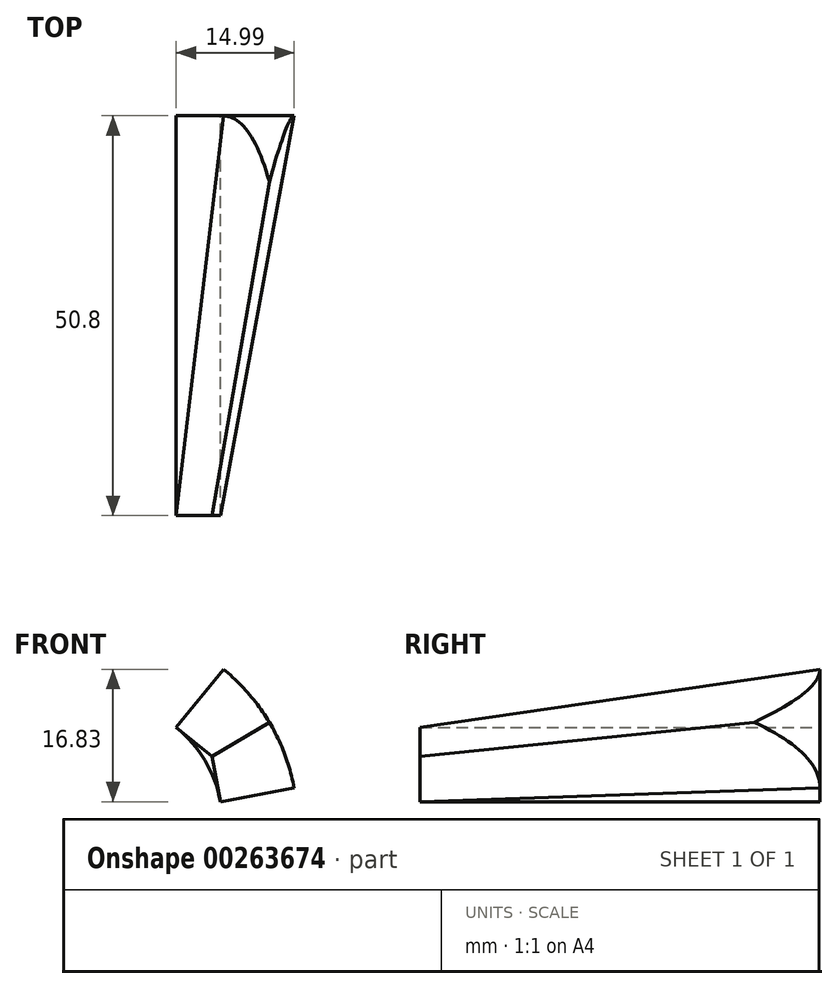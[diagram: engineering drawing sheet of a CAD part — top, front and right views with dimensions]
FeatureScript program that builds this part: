
annotation { "Feature Type Name" : "Feature", "Feature Type Description" : "" }
export const myFeature = defineFeature(function(context is Context, id is Id, definition is map)
    precondition{}
    {
        {
            var Q0;
            Q0=qCreatedBy(makeId("Front.planeOp"),FACE);
            var sketch = newSketch(context, id + "F0", { "sketchPlane" : qUnion([Q0])});
            skCircle(sketch, "E0", {"center": v(0, 0) * mm, "radius": 25.4 * mm});
            skCircle(sketch, "E1", {"center": v(0, 0) * mm, "radius": 15.88 * mm});
            skCircle(sketch, "E2", {"center": v(0, 0) * mm, "radius": 9.53 * mm});
            skLineSegment(sketch, "E3", {"start": v(15.97, 19.75) * mm, "end": v(-15.97, -19.75) * mm});
            skLineSegment(sketch, "E4", {"start": v(-15.93, 19.78) * mm, "end": v(16.53, -19.3) * mm});
            skLineSegment(sketch, "E5", {"start": v(0, 0) * mm, "end": v(-24.97, 4.67) * mm});
            skLineSegment(sketch, "E6", {"start": v(0, 0) * mm, "end": v(-22.89, -11.02) * mm});
            skLineSegment(sketch, "E7", {"start": v(0, 0) * mm, "end": v(24.97, 4.67) * mm});
            skLineSegment(sketch, "E8", {"start": v(0, 0) * mm, "end": v(23.96, -8.44) * mm});
            skSolve(sketch);
        }
        {
            var Q0;
            {var subQ0=sQuery(id+"F0.wireOp",EDGE,"E4");var subQ1=sQuery(id+"F0.wireOp",EDGE,"E0");var subQ2=makeQuery(id+"F0.imprint","INTERSECT",VERTEX,{"disambiguationData":[OD(0.0)],"derivedFrom":[subQ1,subQ0]});Q0=makeQuery(id+"F0.imprint","IMPRINT",FACE,{"disambiguationData":[TD([[makeQuery(id+"F0.imprint","IMPRINT",EDGE,{"disambiguationData":[TD([[subQ2,-1.0]])],"derivedFrom":subQ1}),1.0]])]});}
            var Q1;
            {var subQ0=sQuery(id+"F0.wireOp",EDGE,"E4");var subQ1=sQuery(id+"F0.wireOp",EDGE,"E1");var subQ2=makeQuery(id+"F0.imprint","INTERSECT",VERTEX,{"disambiguationData":[OD(0.0)],"derivedFrom":[subQ1,subQ0]});Q1=makeQuery(id+"F0.imprint","IMPRINT",FACE,{"disambiguationData":[TD([[makeQuery(id+"F0.imprint","IMPRINT",EDGE,{"disambiguationData":[TD([[subQ2,-1.0]])],"derivedFrom":subQ1}),1.0]])]});}
            var Q2;
            {var subQ0=sQuery(id+"F0.wireOp",EDGE,"E3");var subQ1=sQuery(id+"F0.wireOp",EDGE,"E1");var subQ2=makeQuery(id+"F0.imprint","INTERSECT",VERTEX,{"disambiguationData":[OD(0.0)],"derivedFrom":[subQ1,subQ0]});Q2=makeQuery(id+"F0.imprint","IMPRINT",FACE,{"disambiguationData":[TD([[makeQuery(id+"F0.imprint","IMPRINT",EDGE,{"disambiguationData":[TD([[subQ2,-1.0]])],"derivedFrom":subQ1}),1.0]])]});}
            var Q3;
            {var subQ0=sQuery(id+"F0.wireOp",EDGE,"E3");var subQ1=sQuery(id+"F0.wireOp",EDGE,"E1");var subQ2=makeQuery(id+"F0.imprint","INTERSECT",VERTEX,{"disambiguationData":[OD(0.0)],"derivedFrom":[subQ1,subQ0]});Q3=makeQuery(id+"F0.imprint","IMPRINT",FACE,{"disambiguationData":[TD([[makeQuery(id+"F0.imprint","IMPRINT",EDGE,{"disambiguationData":[TD([[subQ2,1.0]])],"derivedFrom":subQ1}),1.0]])]});}
            var Q4;
            {var subQ0=sQuery(id+"F0.wireOp",EDGE,"E7");var subQ1=sQuery(id+"F0.wireOp",EDGE,"E1");var subQ2=makeQuery(id+"F0.imprint","INTERSECT",VERTEX,{"derivedFrom":[subQ1,subQ0]});Q4=makeQuery(id+"F0.imprint","IMPRINT",FACE,{"disambiguationData":[TD([[makeQuery(id+"F0.imprint","IMPRINT",EDGE,{"disambiguationData":[TD([[subQ2,1.0]])],"derivedFrom":subQ1}),1.0]])]});}
            var Q5;
            {var subQ0=sQuery(id+"F0.wireOp",EDGE,"E4");var subQ1=sQuery(id+"F0.wireOp",EDGE,"E1");var subQ2=makeQuery(id+"F0.imprint","INTERSECT",VERTEX,{"disambiguationData":[OD(1.0)],"derivedFrom":[subQ1,subQ0]});Q5=makeQuery(id+"F0.imprint","IMPRINT",FACE,{"disambiguationData":[TD([[makeQuery(id+"F0.imprint","IMPRINT",EDGE,{"disambiguationData":[TD([[subQ2,-1.0]])],"derivedFrom":subQ1}),1.0]])]});}
            var Q6;
            {var subQ0=sQuery(id+"F0.wireOp",EDGE,"E3");var subQ1=sQuery(id+"F0.wireOp",EDGE,"E1");var subQ2=makeQuery(id+"F0.imprint","INTERSECT",VERTEX,{"disambiguationData":[OD(1.0)],"derivedFrom":[subQ1,subQ0]});Q6=makeQuery(id+"F0.imprint","IMPRINT",FACE,{"disambiguationData":[TD([[makeQuery(id+"F0.imprint","IMPRINT",EDGE,{"disambiguationData":[TD([[subQ2,-1.0]])],"derivedFrom":subQ1}),1.0]])]});}
            var Q7;
            {var subQ0=sQuery(id+"F0.wireOp",EDGE,"E6");var subQ1=sQuery(id+"F0.wireOp",EDGE,"E1");var subQ2=makeQuery(id+"F0.imprint","INTERSECT",VERTEX,{"derivedFrom":[subQ1,subQ0]});Q7=makeQuery(id+"F0.imprint","IMPRINT",FACE,{"disambiguationData":[TD([[makeQuery(id+"F0.imprint","IMPRINT",EDGE,{"disambiguationData":[TD([[subQ2,-1.0]])],"derivedFrom":subQ1}),1.0]])]});}
            var Q8;
            {var subQ0=sQuery(id+"F0.wireOp",EDGE,"E5");var subQ1=sQuery(id+"F0.wireOp",EDGE,"E1");var subQ2=makeQuery(id+"F0.imprint","INTERSECT",VERTEX,{"derivedFrom":[subQ1,subQ0]});Q8=makeQuery(id+"F0.imprint","IMPRINT",FACE,{"disambiguationData":[TD([[makeQuery(id+"F0.imprint","IMPRINT",EDGE,{"disambiguationData":[TD([[subQ2,-1.0]])],"derivedFrom":subQ1}),1.0]])]});}
            var Q9;
            {var subQ0=sQuery(id+"F0.wireOp",EDGE,"E3");var subQ1=sQuery(id+"F0.wireOp",EDGE,"E0");var subQ2=makeQuery(id+"F0.imprint","INTERSECT",VERTEX,{"disambiguationData":[OD(0.0)],"derivedFrom":[subQ1,subQ0]});Q9=makeQuery(id+"F0.imprint","IMPRINT",FACE,{"disambiguationData":[TD([[makeQuery(id+"F0.imprint","IMPRINT",EDGE,{"disambiguationData":[TD([[subQ2,1.0]])],"derivedFrom":subQ1}),1.0]])]});}
            var Q10;
            {var subQ0=sQuery(id+"F0.wireOp",EDGE,"E3");var subQ1=sQuery(id+"F0.wireOp",EDGE,"E0");var subQ2=makeQuery(id+"F0.imprint","INTERSECT",VERTEX,{"disambiguationData":[OD(1.0)],"derivedFrom":[subQ1,subQ0]});Q10=makeQuery(id+"F0.imprint","IMPRINT",FACE,{"disambiguationData":[TD([[makeQuery(id+"F0.imprint","IMPRINT",EDGE,{"disambiguationData":[TD([[subQ2,1.0]])],"derivedFrom":subQ1}),1.0]])]});}
            var Q11;
            {var subQ0=sQuery(id+"F0.wireOp",EDGE,"E8");var subQ1=sQuery(id+"F0.wireOp",EDGE,"E0");var subQ2=makeQuery(id+"F0.imprint","INTERSECT",VERTEX,{"derivedFrom":[subQ1,subQ0]});Q11=makeQuery(id+"F0.imprint","IMPRINT",FACE,{"disambiguationData":[TD([[makeQuery(id+"F0.imprint","IMPRINT",EDGE,{"disambiguationData":[TD([[subQ2,1.0]])],"derivedFrom":subQ1}),1.0]])]});}
            extrude(context, id + "F1", {"entities" : qUnion([Q0, Q1, Q2, Q3, Q4, Q5, Q6, Q7, Q8, Q9, Q10, Q11]), "depth" : 50.8 * mm});
        }
        {
            var Q0;
            Q0=makeQuery(id+"F1.opExtrude","CAP_FACE",FACE,{"disambiguationData":[OSD([sQuery(id+"F0.wireOp",EDGE,"E0"),sQuery(id+"F0.wireOp",EDGE,"E1"),sQuery(id+"F0.wireOp",EDGE,"E2"),sQuery(id+"F0.wireOp",EDGE,"E3"),sQuery(id+"F0.wireOp",EDGE,"E4"),sQuery(id+"F0.wireOp",EDGE,"E5"),sQuery(id+"F0.wireOp",EDGE,"E6"),sQuery(id+"F0.wireOp",EDGE,"E7"),sQuery(id+"F0.wireOp",EDGE,"E8")])],"isStart":false});
            var sketch = newSketch(context, id + "F2", { "sketchPlane" : qUnion([Q0])});
            skLineSegment(sketch, "E9", {"start": v(0, 0) * mm, "end": v(-9.53, 0) * mm});
            skLineSegment(sketch, "E10", {"start": v(0, 0) * mm, "end": v(9.53, 0) * mm});
            skLineSegment(sketch, "E11", {"start": v(0, 0) * mm, "end": v(0, 9.53) * mm});
            skLineSegment(sketch, "E12", {"start": v(0, 0) * mm, "end": v(0, -9.53) * mm});
            skLineSegment(sketch, "E13", {"start": v(0, 0) * mm, "end": v(6.74, 6.74) * mm});
            skLineSegment(sketch, "E14", {"start": v(0, 0) * mm, "end": v(-6.74, 6.74) * mm});
            skLineSegment(sketch, "E15", {"start": v(-6.74, 6.74) * mm, "end": v(-9.53, 9.52) * mm});
            skLineSegment(sketch, "E16", {"start": v(-9.53, 9.52) * mm, "end": v(-9.53, 0) * mm});
            skLineSegment(sketch, "E17", {"start": v(6.74, 6.74) * mm, "end": v(9.53, 9.52) * mm});
            skLineSegment(sketch, "E18", {"start": v(9.53, 9.52) * mm, "end": v(9.53, 0) * mm});
            skSolve(sketch);
        }
        {
            var Q0;
            {var subQ0=sQuery(id+"F2.wireOp",EDGE,"E15");Q0=makeQuery(id+"F2.imprint","IMPRINT",FACE,{"disambiguationData":[TD([[makeQuery(id+"F2.imprint","IMPRINT",EDGE,{"derivedFrom":subQ0}),1.0]])]});}
            var Q1;
            {var subQ0=sQuery(id+"F2.wireOp",EDGE,"E17");Q1=makeQuery(id+"F2.imprint","IMPRINT",FACE,{"disambiguationData":[TD([[makeQuery(id+"F2.imprint","IMPRINT",EDGE,{"derivedFrom":subQ0}),-1.0]])]});}
            extrude(context, id + "F3", {"entities" : qUnion([Q0, Q1]), "operationType" : NewBodyOperationType.REMOVE, "oppositeDirection" : true, "depth" : 50.8 * mm});
        }
        {
            var Q0;
            {var subQ0=sQuery(id+"F0.wireOp",EDGE,"E3");Q0=makeQuery(id+"F1.opExtrude","SWEPT_FACE",FACE,{"disambiguationData":[OSD([subQ0]),TDD([makeQuery(id+"F0.imprint","IMPRINT",EDGE,{"disambiguationData":[TD([[makeQuery(id+"F0.imprint","INTERSECT",VERTEX,{"disambiguationData":[OD(1.0)],"derivedFrom":[sQuery(id+"F0.wireOp",EDGE,"E0"),subQ0]}),1.0]])],"derivedFrom":subQ0})])]});}
            var sketch = newSketch(context, id + "F4", { "sketchPlane" : qUnion([Q0])});
            skLineSegment(sketch, "E19", {"start": v(-50.8, -15.88) * mm, "end": v(0, -25.4) * mm});
            skSolve(sketch);
        }
        {
            var Q0;
            Q0=makeQuery(id+"F4.imprint","IMPRINT",FACE,{"disambiguationData":[TD([[makeQuery(id+"F4.imprint","IMPRINT",EDGE,{"derivedFrom":sQuery(id+"F4.wireOp",EDGE,"E19")}),-1.0]])]});
            extrude(context, id + "F5", {"entities" : qUnion([Q0]), "operationType" : NewBodyOperationType.REMOVE, "endBound" : BoundingType.THROUGH_ALL, "oppositeDirection" : true, "depth" : 25.4 * mm});
        }
        {
            var Q0;
            Q0=makeQuery(id+"F1.opExtrude","SWEPT_FACE",FACE,{"disambiguationData":[OSD([sQuery(id+"F0.wireOp",EDGE,"E6")])]});
            var sketch = newSketch(context, id + "F6", { "sketchPlane" : qUnion([Q0])});
            skLineSegment(sketch, "E20", {"start": v(-15.87, -50.8) * mm, "end": v(-25.4, 0) * mm});
            skSolve(sketch);
        }
        {
            var Q0;
            Q0 = qSketchRegion(id + "F6", true);
            var Q1;
            Q1=makeQuery(id+"F6.imprint","IMPRINT",FACE,{"disambiguationData":[TD([[makeQuery(id+"F6.imprint","IMPRINT",EDGE,{"derivedFrom":sQuery(id+"F6.wireOp",EDGE,"E20")}),1.0]])]});
            extrude(context, id + "F7", {"entities" : qUnion([Q0, Q1]), "operationType" : NewBodyOperationType.REMOVE, "endBound" : BoundingType.THROUGH_ALL, "oppositeDirection" : true, "depth" : 25.4 * mm});
        }
        {
            var Q0;
            {var subQ0=sQuery(id+"F0.wireOp",EDGE,"E4");Q0=makeQuery(id+"F1.opExtrude","SWEPT_FACE",FACE,{"disambiguationData":[OSD([subQ0]),TDD([makeQuery(id+"F0.imprint","IMPRINT",EDGE,{"disambiguationData":[TD([[makeQuery(id+"F0.imprint","INTERSECT",VERTEX,{"disambiguationData":[OD(1.0)],"derivedFrom":[sQuery(id+"F0.wireOp",EDGE,"E0"),subQ0]}),1.0]])],"derivedFrom":subQ0})])]});}
            var sketch = newSketch(context, id + "F8", { "sketchPlane" : qUnion([Q0])});
            skLineSegment(sketch, "E21", {"start": v(50.8, -15.87) * mm, "end": v(0, -25.4) * mm});
            skSolve(sketch);
        }
        {
            var Q0;
            Q0 = qSketchRegion(id + "F8", true);
            var Q1;
            Q1=makeQuery(id+"F8.imprint","IMPRINT",FACE,{"disambiguationData":[TD([[makeQuery(id+"F8.imprint","IMPRINT",EDGE,{"derivedFrom":sQuery(id+"F8.wireOp",EDGE,"E21")}),1.0]])]});
            extrude(context, id + "F9", {"entities" : qUnion([Q0, Q1]), "operationType" : NewBodyOperationType.REMOVE, "endBound" : BoundingType.THROUGH_ALL, "oppositeDirection" : true, "depth" : 25.4 * mm});
        }
        {
            var Q0;
            Q0=makeQuery(id+"F1.opExtrude","SWEPT_FACE",FACE,{"disambiguationData":[OSD([sQuery(id+"F0.wireOp",EDGE,"E8")])]});
            var sketch = newSketch(context, id + "F10", { "sketchPlane" : qUnion([Q0])});
            skLineSegment(sketch, "E22", {"start": v(15.88, -50.8) * mm, "end": v(25.4, 0) * mm});
            skSolve(sketch);
        }
        {
            var Q0;
            Q0 = qSketchRegion(id + "F10", true);
            var Q1;
            Q1=makeQuery(id+"F10.imprint","IMPRINT",FACE,{"disambiguationData":[TD([[makeQuery(id+"F10.imprint","IMPRINT",EDGE,{"derivedFrom":sQuery(id+"F10.wireOp",EDGE,"E22")}),-1.0]])]});
            extrude(context, id + "F11", {"entities" : qUnion([Q0, Q1]), "operationType" : NewBodyOperationType.REMOVE, "endBound" : BoundingType.THROUGH_ALL, "oppositeDirection" : true, "depth" : 25.4 * mm});
        }
        {
            var Q0;
            {var subQ0=sQuery(id+"F0.wireOp",EDGE,"E4");Q0=makeQuery(id+"F1.opExtrude","SWEPT_FACE",FACE,{"disambiguationData":[OSD([subQ0]),TDD([makeQuery(id+"F0.imprint","IMPRINT",EDGE,{"disambiguationData":[TD([[makeQuery(id+"F0.imprint","INTERSECT",VERTEX,{"disambiguationData":[OD(0.0)],"derivedFrom":[sQuery(id+"F0.wireOp",EDGE,"E0"),subQ0]}),-1.0]])],"derivedFrom":subQ0})])]});}
            var sketch = newSketch(context, id + "F12", { "sketchPlane" : qUnion([Q0])});
            skLineSegment(sketch, "E23", {"start": v(-50.8, 15.87) * mm, "end": v(0, 25.4) * mm});
            skSolve(sketch);
        }
        {
            var Q0;
            Q0=makeQuery(id+"F12.imprint","IMPRINT",FACE,{"disambiguationData":[TD([[makeQuery(id+"F12.imprint","IMPRINT",EDGE,{"derivedFrom":sQuery(id+"F12.wireOp",EDGE,"E23")}),1.0]])]});
            extrude(context, id + "F13", {"entities" : qUnion([Q0]), "operationType" : NewBodyOperationType.REMOVE, "endBound" : BoundingType.THROUGH_ALL, "oppositeDirection" : true, "depth" : 25.4 * mm});
        }
        {
            var Q0;
            Q0=makeQuery(id+"F1.opExtrude","SWEPT_FACE",FACE,{"disambiguationData":[OSD([sQuery(id+"F0.wireOp",EDGE,"E5")])]});
            var sketch = newSketch(context, id + "F14", { "sketchPlane" : qUnion([Q0])});
            skLineSegment(sketch, "E24", {"start": v(-15.88, 50.8) * mm, "end": v(-25.4, 0) * mm});
            skSolve(sketch);
        }
        {
            var Q0;
            Q0 = qSketchRegion(id + "F14", true);
            var Q1;
            Q1=makeQuery(id+"F14.imprint","IMPRINT",FACE,{"disambiguationData":[TD([[makeQuery(id+"F14.imprint","IMPRINT",EDGE,{"derivedFrom":sQuery(id+"F14.wireOp",EDGE,"E24")}),-1.0]])]});
            extrude(context, id + "F15", {"entities" : qUnion([Q0, Q1]), "operationType" : NewBodyOperationType.REMOVE, "endBound" : BoundingType.THROUGH_ALL, "oppositeDirection" : true, "depth" : 25.4 * mm});
        }
        {
            var Q0;
            Q0=makeQuery(id+"F1.opExtrude","SWEPT_FACE",FACE,{"disambiguationData":[OSD([sQuery(id+"F0.wireOp",EDGE,"E7")])]});
            var sketch = newSketch(context, id + "F16", { "sketchPlane" : qUnion([Q0])});
            skLineSegment(sketch, "E25", {"start": v(15.87, 50.8) * mm, "end": v(25.4, 0) * mm});
            skSolve(sketch);
        }
        {
            var Q0;
            Q0 = qSketchRegion(id + "F16", true);
            var Q1;
            Q1=makeQuery(id+"F16.imprint","IMPRINT",FACE,{"disambiguationData":[TD([[makeQuery(id+"F16.imprint","IMPRINT",EDGE,{"derivedFrom":sQuery(id+"F16.wireOp",EDGE,"E25")}),1.0]])]});
            extrude(context, id + "F17", {"entities" : qUnion([Q0, Q1]), "operationType" : NewBodyOperationType.REMOVE, "endBound" : BoundingType.THROUGH_ALL, "oppositeDirection" : true, "depth" : 25.4 * mm});
        }
        {
            var Q0;
            {var subQ0=sQuery(id+"F0.wireOp",EDGE,"E3");Q0=makeQuery(id+"F1.opExtrude","SWEPT_FACE",FACE,{"disambiguationData":[OSD([subQ0]),TDD([makeQuery(id+"F0.imprint","IMPRINT",EDGE,{"disambiguationData":[TD([[makeQuery(id+"F0.imprint","INTERSECT",VERTEX,{"disambiguationData":[OD(0.0)],"derivedFrom":[sQuery(id+"F0.wireOp",EDGE,"E0"),subQ0]}),-1.0]])],"derivedFrom":subQ0})])]});}
            var sketch = newSketch(context, id + "F18", { "sketchPlane" : qUnion([Q0])});
            skLineSegment(sketch, "E26", {"start": v(50.8, 15.88) * mm, "end": v(0, 25.4) * mm});
            skSolve(sketch);
        }
        {
            var Q0;
            Q0 = qSketchRegion(id + "F18", true);
            var Q1;
            Q1=makeQuery(id+"F18.imprint","IMPRINT",FACE,{"disambiguationData":[TD([[makeQuery(id+"F18.imprint","IMPRINT",EDGE,{"derivedFrom":sQuery(id+"F18.wireOp",EDGE,"E26")}),-1.0]])]});
            extrude(context, id + "F19", {"entities" : qUnion([Q0, Q1]), "operationType" : NewBodyOperationType.REMOVE, "endBound" : BoundingType.THROUGH_ALL, "oppositeDirection" : true, "depth" : 25.4 * mm});
        }
        {
            var Q0;
            Q0=makeQuery(id+"F13.boolean.opBoolean","SPLIT",BODY,{"disambiguationData":[OD(1.0)],"derivedFrom":makeQuery(id+"F1.opExtrude","SWEPT_BODY",BODY,{"disambiguationData":[OSD([sQuery(id+"F0.wireOp",EDGE,"E0"),sQuery(id+"F0.wireOp",EDGE,"E1"),sQuery(id+"F0.wireOp",EDGE,"E2"),sQuery(id+"F0.wireOp",EDGE,"E3"),sQuery(id+"F0.wireOp",EDGE,"E4"),sQuery(id+"F0.wireOp",EDGE,"E5"),sQuery(id+"F0.wireOp",EDGE,"E6"),sQuery(id+"F0.wireOp",EDGE,"E7"),sQuery(id+"F0.wireOp",EDGE,"E8")])]})});
            deleteBodies(context, id + "F20", {"entities" : qUnion([Q0])});
        }
    });
